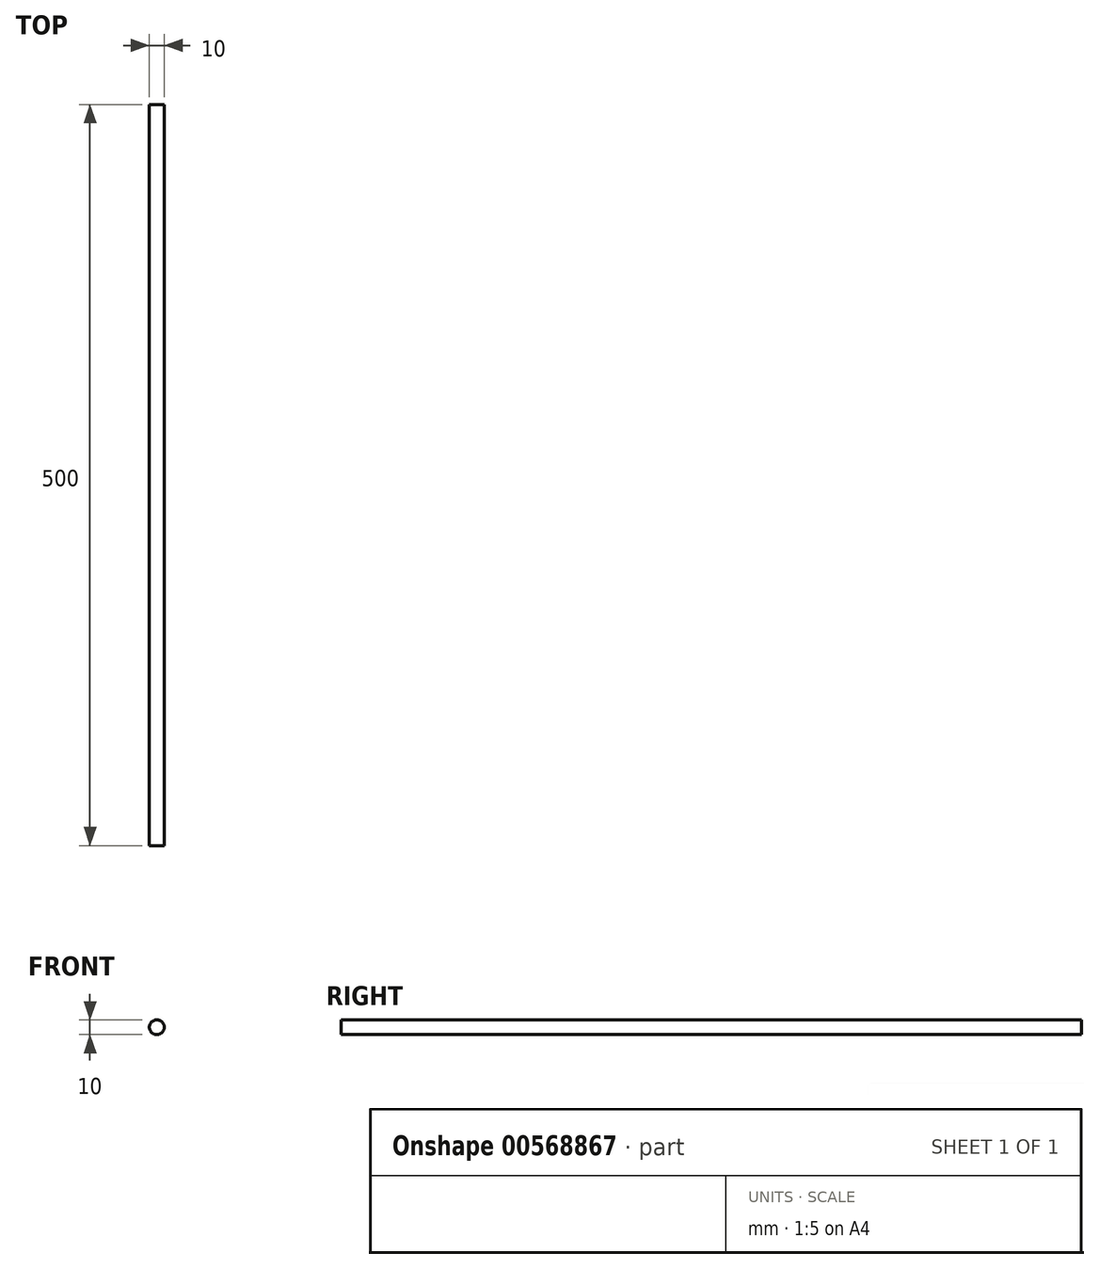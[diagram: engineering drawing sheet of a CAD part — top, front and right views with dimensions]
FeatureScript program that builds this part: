
annotation { "Feature Type Name" : "Feature", "Feature Type Description" : "" }
export const myFeature = defineFeature(function(context is Context, id is Id, definition is map)
    precondition{}
    {
        {
            var Q0;
            Q0=qCreatedBy(makeId("Front.planeOp"),FACE);
            var sketch = newSketch(context, id + "F0", { "sketchPlane" : qUnion([Q0])});
            skCircle(sketch, "E0", {"center": v(0, 0) * mm, "radius": 5 * mm});
            skSolve(sketch);
        }
        {
            var Q0;
            Q0 = qSketchRegion(id + "F0", true);
            extrude(context, id + "F1", {"entities" : qUnion([Q0]), "depth" : 500 * mm, "offsetDistance" : 25 * mm, "symmetric" : true});
        }
    });
